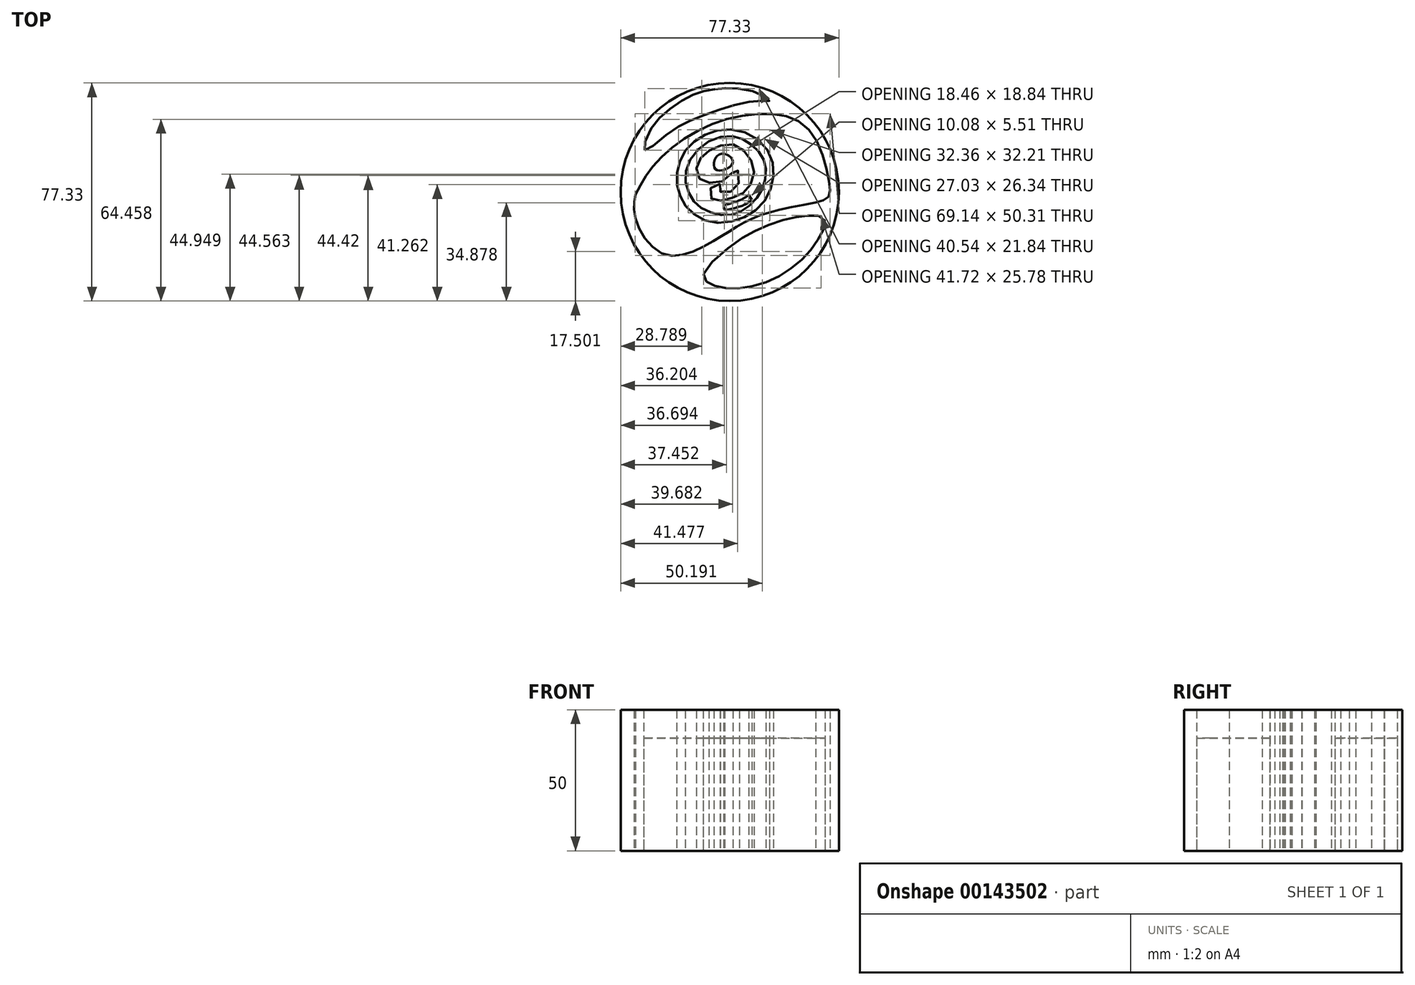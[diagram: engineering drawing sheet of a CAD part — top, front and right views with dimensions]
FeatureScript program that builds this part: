
annotation { "Feature Type Name" : "Feature", "Feature Type Description" : "" }
export const myFeature = defineFeature(function(context is Context, id is Id, definition is map)
    precondition{}
    {
        {
            var Q0;
            Q0=qCreatedBy(makeId("Top.planeOp"),FACE);
            var sketch = newSketch(context, id + "F0", { "sketchPlane" : qUnion([Q0])});
            skCircle(sketch, "E0", {"center": v(-45.37, -32.33) * mm, "radius": 38.67 * mm});
            skPoint(sketch, "E0.first.point", {"position": v(-62.48, 2.33) * mm});
            skPoint(sketch, "E0.second.point", {"position": v(-27.97, -66.87) * mm});
            skPoint(sketch, "E0.third.point", {"position": v(-8.34, -21.18) * mm});
            skPoint(sketch, "E1", {"position": v(-78.73, -33.2) * mm});
            skPoint(sketch, "E2", {"position": v(-78.73, -42) * mm});
            skPoint(sketch, "E3", {"position": v(-68.4, -54.51) * mm});
            skPoint(sketch, "E4", {"position": v(-53, -50.8) * mm});
            skPoint(sketch, "E5", {"position": v(-33.04, -40.13) * mm});
            skPoint(sketch, "E6", {"position": v(-14.94, -36.07) * mm});
            skPoint(sketch, "E7", {"position": v(-10.37, -27.61) * mm});
            skPoint(sketch, "E8", {"position": v(-17.48, -10.02) * mm});
            skPoint(sketch, "E9", {"position": v(-34.23, -4.6) * mm});
            skPoint(sketch, "E10", {"position": v(-56.9, -10.7) * mm});
            skFitSpline(sketch, "E11", {"points": [v(-78.73, -33.2) * mm, v(-78.73, -42) * mm, v(-68.4, -54.51) * mm, v(-53, -50.8) * mm, v(-42.69, -44.53) * mm, v(-33.04, -40.13) * mm, v(-14.94, -36.07) * mm], "startDerivative": vector(-10.86, -59.4) * mm, "endDerivative": vector(100.31, 18.72) * mm});
            skPoint(sketch, "E12", {"position": v(-10.37, -34.04) * mm});
            skFitSpline(sketch, "E13", {"points": [v(-14.94, -36.07) * mm, v(-10.37, -34.04) * mm, v(-10.37, -27.61) * mm, v(-17.48, -10.02) * mm, v(-34.23, -4.6) * mm, v(-56.9, -10.7) * mm, v(-72.64, -23.38) * mm, v(-78.73, -33.2) * mm], "startDerivative": vector(65.07, 15.9) * mm, "endDerivative": vector(-38.3, -73.96) * mm});
            skPoint(sketch, "E14", {"position": v(-75.51, -17.46) * mm});
            skPoint(sketch, "E15", {"position": v(-73.99, -11.03) * mm});
            skPoint(sketch, "E16", {"position": v(-67.22, -3.42) * mm});
            skPoint(sketch, "E17", {"position": v(-58.42, 2.17) * mm});
            skPoint(sketch, "E18", {"position": v(-52, 3.86) * mm});
            skPoint(sketch, "E19", {"position": v(-44.89, 4.53) * mm});
            skPoint(sketch, "E20", {"position": v(-34.4, 2.33) * mm});
            skPoint(sketch, "E21", {"position": v(-31.35, 0) * mm});
            skPoint(sketch, "E22", {"position": v(-34.23, 0) * mm});
            skPoint(sketch, "E23", {"position": v(-45.23, -1.9) * mm});
            skPoint(sketch, "E24", {"position": v(-57.92, -6.46) * mm});
            skPoint(sketch, "E25", {"position": v(-67.9, -12.05) * mm});
            skPoint(sketch, "E26", {"position": v(-54.7, -61.45) * mm});
            skPoint(sketch, "E27", {"position": v(-43.87, -50.62) * mm});
            skPoint(sketch, "E28", {"position": v(-34.74, -45.38) * mm});
            skPoint(sketch, "E29", {"position": v(-24.58, -41.83) * mm});
            skPoint(sketch, "E30", {"position": v(-17.99, -40.81) * mm});
            skPoint(sketch, "E31", {"position": v(-13.08, -40.98) * mm});
            skPoint(sketch, "E32", {"position": v(-11.56, -43.35) * mm});
            skPoint(sketch, "E33", {"position": v(-13.59, -48.42) * mm});
            skPoint(sketch, "E34", {"position": v(-17.99, -54.51) * mm});
            skPoint(sketch, "E35", {"position": v(-24.75, -60.27) * mm});
            skPoint(sketch, "E36", {"position": v(-33.38, -64.67) * mm});
            skPoint(sketch, "E37", {"position": v(-42.86, -66.53) * mm});
            skPoint(sketch, "E38", {"position": v(-50.64, -66.02) * mm});
            skPoint(sketch, "E39", {"position": v(-53.52, -64.16) * mm});
            skFitSpline(sketch, "E40", {"points": [v(-75.51, -17.46) * mm, v(-73.99, -11.03) * mm, v(-67.22, -3.42) * mm, v(-58.42, 2.17) * mm, v(-52, 3.86) * mm, v(-44.89, 4.53) * mm, v(-34.4, 2.33) * mm, v(-31.35, 0) * mm, v(-34.23, 0) * mm, v(-45.23, -1.9) * mm, v(-57.92, -6.46) * mm, v(-67.9, -12.05) * mm, v(-75.51, -17.46) * mm]});
            skFitSpline(sketch, "E41", {"points": [v(-54.7, -61.45) * mm, v(-53.52, -64.16) * mm, v(-49.29, -66.02) * mm, v(-42.86, -66.53) * mm, v(-33.38, -64.67) * mm, v(-24.75, -60.27) * mm, v(-17.99, -54.51) * mm, v(-13.59, -48.42) * mm, v(-11.56, -43.35) * mm, v(-13.08, -40.98) * mm, v(-17.99, -40.81) * mm, v(-24.58, -41.83) * mm, v(-34.74, -45.38) * mm, v(-43.87, -50.62) * mm, v(-54.7, -61.45) * mm]});
            skPoint(sketch, "E42.second.point", {"position": v(-40.15, -41.32) * mm});
            skPoint(sketch, "E43", {"position": v(-54.02, -12.05) * mm});
            skPoint(sketch, "E44", {"position": v(-64, -25.58) * mm});
            skPoint(sketch, "E45", {"position": v(-63.16, -33.2) * mm});
            skPoint(sketch, "E46", {"position": v(-58.76, -39.63) * mm});
            skPoint(sketch, "E47", {"position": v(-50.64, -43.18) * mm});
            skPoint(sketch, "E48", {"position": v(-32.88, -35.23) * mm});
            skPoint(sketch, "E49", {"position": v(-29.83, -25.41) * mm});
            skPoint(sketch, "E50", {"position": v(-33.38, -15.6) * mm});
            skPoint(sketch, "E51", {"position": v(-44.21, -10.19) * mm});
            skPoint(sketch, "E52", {"position": v(-60.96, -17.46) * mm});
            skPoint(sketch, "E53", {"position": v(-54.2, -15.26) * mm});
            skPoint(sketch, "E54", {"position": v(-60.8, -24.4) * mm});
            skPoint(sketch, "E55", {"position": v(-59.78, -32.86) * mm});
            skPoint(sketch, "E56", {"position": v(-55.55, -37.93) * mm});
            skPoint(sketch, "E57", {"position": v(-47.93, -40.47) * mm});
            skPoint(sketch, "E58", {"position": v(-41.5, -39.29) * mm});
            skPoint(sketch, "E59", {"position": v(-35.41, -34.04) * mm});
            skPoint(sketch, "E60", {"position": v(-32.7, -27.44) * mm});
            skPoint(sketch, "E61", {"position": v(-33.38, -20.85) * mm});
            skPoint(sketch, "E62", {"position": v(-37.44, -15.77) * mm});
            skPoint(sketch, "E63", {"position": v(-44.38, -12.55) * mm});
            skPoint(sketch, "E64", {"position": v(-44.21, -21.52) * mm});
            skPoint(sketch, "E65", {"position": v(-47.26, -18.81) * mm});
            skPoint(sketch, "E66", {"position": v(-50.47, -20.34) * mm});
            skPoint(sketch, "E67", {"position": v(-50.47, -24.23) * mm});
            skPoint(sketch, "E68", {"position": v(-46.75, -24.23) * mm});
            skPoint(sketch, "E69", {"position": v(-43.03, -24.23) * mm});
            skPoint(sketch, "E70", {"position": v(-42.01, -28.46) * mm});
            skPoint(sketch, "E71", {"position": v(-48.78, -32.01) * mm});
            skPoint(sketch, "E72", {"position": v(-52.5, -31.5) * mm});
            skPoint(sketch, "E73", {"position": v(-51.15, -35.23) * mm});
            skPoint(sketch, "E74", {"position": v(-47.26, -35.06) * mm});
            skPoint(sketch, "E75", {"position": v(-42.01, -33.53) * mm});
            skPoint(sketch, "E76", {"position": v(-38.29, -30.15) * mm});
            skPoint(sketch, "E77", {"position": v(-36.77, -24.4) * mm});
            skPoint(sketch, "E78", {"position": v(-39.14, -18.98) * mm});
            skPoint(sketch, "E79", {"position": v(-43.7, -15.6) * mm});
            skPoint(sketch, "E80", {"position": v(-49.8, -16.28) * mm});
            skPoint(sketch, "E81", {"position": v(-54.53, -18.98) * mm});
            skPoint(sketch, "E82", {"position": v(-57.07, -23.21) * mm});
            skPoint(sketch, "E83", {"position": v(-56.06, -27.61) * mm});
            skPoint(sketch, "E84", {"position": v(-51.66, -29.14) * mm});
            skPoint(sketch, "E85", {"position": v(-46.07, -27.27) * mm});
            skFitSpline(sketch, "E86", {"points": [v(-44.21, -21.52) * mm, v(-47.26, -18.81) * mm, v(-50.47, -20.34) * mm, v(-50.47, -24.23) * mm, v(-46.75, -24.23) * mm, v(-44.21, -21.52) * mm]});
            skPoint(sketch, "E87", {"position": v(-48.78, -29.47) * mm});
            skFitSpline(sketch, "E88", {"points": [v(-48.78, -29.47) * mm, v(-48.78, -32.01) * mm, v(-45.37, -32.33) * mm, v(-42.01, -28.46) * mm, v(-43.03, -24.23) * mm, v(-46.07, -27.27) * mm, v(-51.66, -29.14) * mm, v(-56.06, -27.61) * mm, v(-57.07, -23.21) * mm, v(-54.53, -18.98) * mm, v(-49.8, -16.28) * mm, v(-43.7, -15.6) * mm, v(-39.14, -18.98) * mm, v(-36.77, -24.4) * mm, v(-38.29, -30.15) * mm, v(-42.01, -33.53) * mm, v(-47.26, -35.06) * mm, v(-51.15, -35.23) * mm, v(-52.5, -31.5) * mm, v(-48.78, -29.47) * mm]});
            skFitSpline(sketch, "E89", {"points": [v(-40.15, -41.32) * mm, v(-32.88, -35.23) * mm, v(-29.83, -25.41) * mm, v(-33.38, -15.6) * mm, v(-44.21, -10.19) * mm, v(-54.02, -12.05) * mm, v(-60.96, -17.46) * mm, v(-64, -25.58) * mm, v(-63.16, -33.2) * mm, v(-58.76, -39.63) * mm, v(-50.64, -43.18) * mm, v(-40.15, -41.32) * mm]});
            skFitSpline(sketch, "E90", {"points": [v(-41.5, -39.29) * mm, v(-35.41, -34.04) * mm, v(-32.7, -27.44) * mm, v(-33.38, -20.85) * mm, v(-37.44, -15.77) * mm, v(-44.38, -12.55) * mm, v(-54.2, -15.26) * mm, v(-60.8, -24.4) * mm, v(-59.78, -32.86) * mm, v(-55.55, -37.93) * mm, v(-47.93, -40.47) * mm, v(-41.5, -39.29) * mm]});
            skPoint(sketch, "E91", {"position": v(-47.6, -37.09) * mm});
            skPoint(sketch, "E92", {"position": v(-38.63, -33.37) * mm});
            skFitSpline(sketch, "E93", {"points": [v(-47.6, -37.09) * mm, v(-41.36, -35.06) * mm, v(-38.63, -33.37) * mm], "startDerivative": vector(11.76, 3.26) * mm, "endDerivative": vector(5.83, 4.24) * mm});
            skPoint(sketch, "E94", {"position": v(-37.51, -35.16) * mm});
            skPoint(sketch, "E95", {"position": v(-47.18, -38.88) * mm});
            skLineSegment(sketch, "E96", {"start": v(-38.63, -33.37) * mm, "end": v(-37.51, -35.16) * mm});
            skLineSegment(sketch, "E97", {"start": v(-47.6, -37.09) * mm, "end": v(-47.18, -38.88) * mm});
            skFitSpline(sketch, "E98", {"points": [v(-47.18, -38.88) * mm, v(-39.93, -36.79) * mm, v(-37.51, -35.16) * mm], "startDerivative": vector(13.44, 3.12) * mm, "endDerivative": vector(5.26, 4.43) * mm});
            skSolve(sketch);
        }
        {
            var Q0;
            Q0=makeQuery(id+"F0.imprint","IMPRINT",FACE,{"disambiguationData":[TD([[makeQuery(id+"F0.imprint","IMPRINT",EDGE,{"derivedFrom":sQuery(id+"F0.wireOp",EDGE,"E0")}),1.0]])]});
            extrude(context, id + "F1", {"entities" : qUnion([Q0]), "depth" : 50 * mm});
        }
        {
            var Q0;
            Q0=makeQuery(id+"F0.imprint","IMPRINT",FACE,{"disambiguationData":[TD([[makeQuery(id+"F0.imprint","IMPRINT",EDGE,{"derivedFrom":sQuery(id+"F0.wireOp",EDGE,"E11")}),1.0]])]});
            extrude(context, id + "F2", {"entities" : qUnion([Q0]), "depth" : 50 * mm});
        }
        {
            var Q0;
            Q0=makeQuery(id+"F0.imprint","IMPRINT",FACE,{"disambiguationData":[TD([[makeQuery(id+"F0.imprint","IMPRINT",EDGE,{"derivedFrom":sQuery(id+"F0.wireOp",EDGE,"E89")}),1.0]])]});
            extrude(context, id + "F3", {"entities" : qUnion([Q0]), "depth" : 50 * mm});
        }
        {
            var Q0;
            Q0=makeQuery(id+"F0.imprint","IMPRINT",FACE,{"disambiguationData":[TD([[makeQuery(id+"F0.imprint","IMPRINT",EDGE,{"derivedFrom":sQuery(id+"F0.wireOp",EDGE,"E86")}),-1.0]])]});
            extrude(context, id + "F4", {"entities" : qUnion([Q0]), "depth" : 50 * mm});
        }
        {
            var Q0;
            Q0=makeQuery(id+"F0.imprint","IMPRINT",FACE,{"disambiguationData":[TD([[makeQuery(id+"F0.imprint","IMPRINT",EDGE,{"derivedFrom":sQuery(id+"F0.wireOp",EDGE,"E88")}),1.0]])]});
            extrude(context, id + "F5", {"entities" : qUnion([Q0]), "depth" : 50 * mm});
        }
        {
            var Q0;
            Q0=makeQuery(id+"F0.imprint","IMPRINT",FACE,{"disambiguationData":[TD([[makeQuery(id+"F0.imprint","IMPRINT",EDGE,{"derivedFrom":sQuery(id+"F0.wireOp",EDGE,"E86")}),1.0]])]});
            extrude(context, id + "F6", {"entities" : qUnion([Q0]), "depth" : 50 * mm});
        }
        {
            var Q0;
            Q0=makeQuery(id+"F0.imprint","IMPRINT",FACE,{"disambiguationData":[TD([[makeQuery(id+"F0.imprint","IMPRINT",EDGE,{"derivedFrom":sQuery(id+"F0.wireOp",EDGE,"E93")}),-1.0]])]});
            extrude(context, id + "F7", {"entities" : qUnion([Q0]), "depth" : 50 * mm});
        }
        {
            var Q0;
            Q0=makeQuery(id+"F0.imprint","IMPRINT",FACE,{"disambiguationData":[TD([[makeQuery(id+"F0.imprint","IMPRINT",EDGE,{"derivedFrom":sQuery(id+"F0.wireOp",EDGE,"E41")}),1.0]])]});
            extrude(context, id + "F8", {"entities" : qUnion([Q0]), "depth" : 40 * mm});
        }
        {
            var Q0;
            Q0=makeQuery(id+"F0.imprint","IMPRINT",FACE,{"disambiguationData":[TD([[makeQuery(id+"F0.imprint","IMPRINT",EDGE,{"derivedFrom":sQuery(id+"F0.wireOp",EDGE,"E40")}),-1.0]])]});
            extrude(context, id + "F9", {"entities" : qUnion([Q0]), "depth" : 40 * mm});
        }
    });
